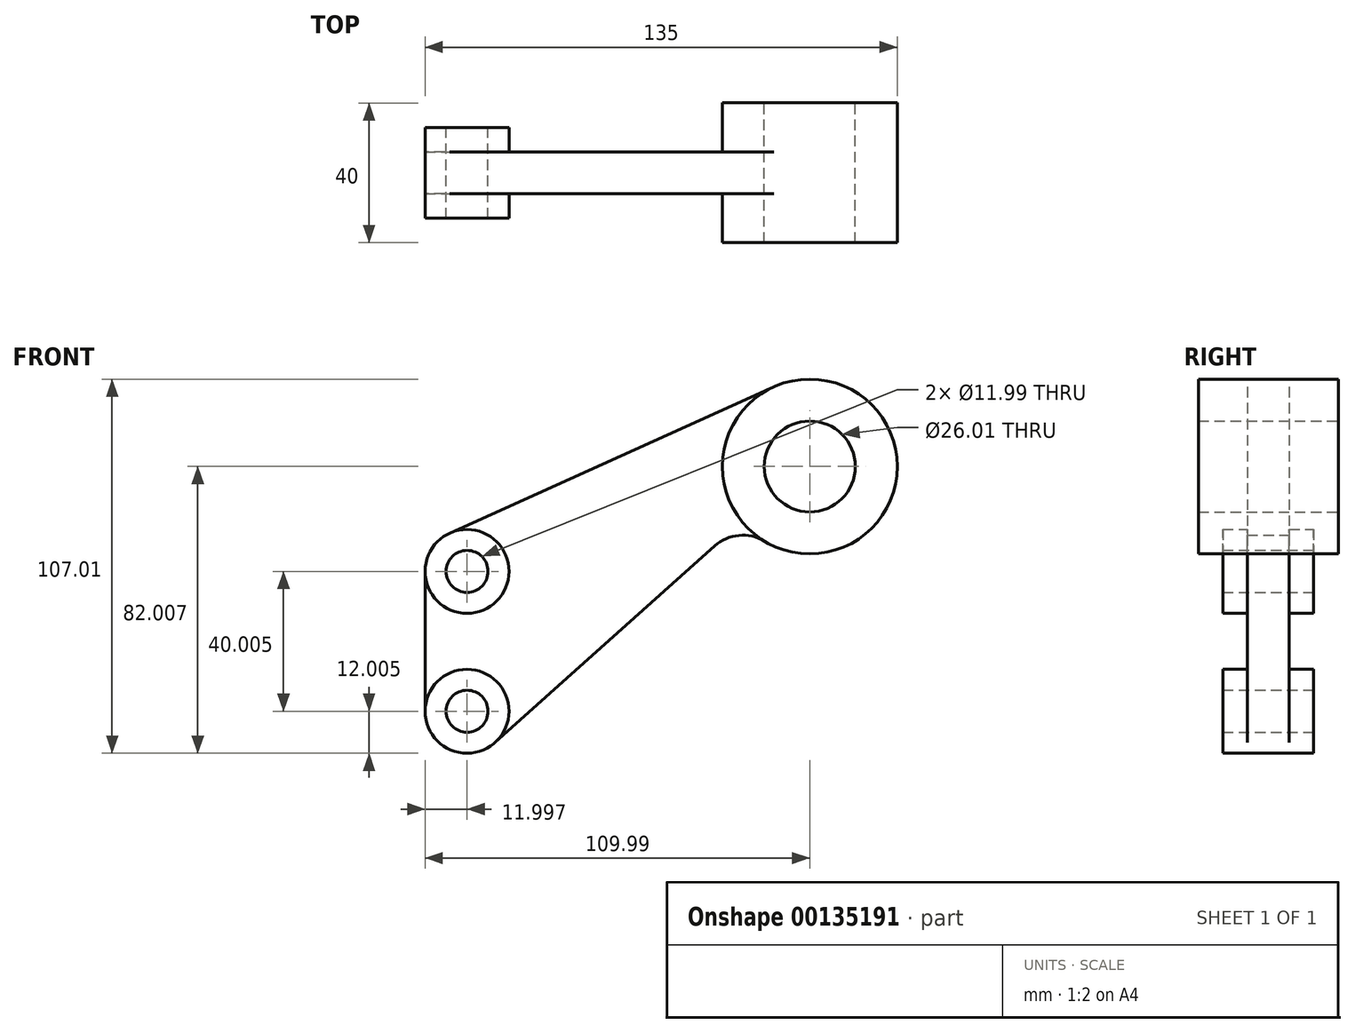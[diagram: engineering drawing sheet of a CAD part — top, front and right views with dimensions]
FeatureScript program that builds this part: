
annotation { "Feature Type Name" : "Feature", "Feature Type Description" : "" }
export const myFeature = defineFeature(function(context is Context, id is Id, definition is map)
    precondition{}
    {
        {
            var Q0;
            Q0=qCreatedBy(makeId("Front.planeOp"),FACE);
            var sketch = newSketch(context, id + "F0", { "sketchPlane" : qUnion([Q0])});
            skCircle(sketch, "E0", {"center": v(0, 53.52) * mm, "radius": 25 * mm});
            skCircle(sketch, "E1", {"center": v(0, 53.52) * mm, "radius": 13 * mm});
            skCircle(sketch, "E2", {"center": v(-98, 23.52) * mm, "radius": 12 * mm});
            skCircle(sketch, "E3", {"center": v(-98, 23.52) * mm, "radius": 6 * mm});
            skLineSegment(sketch, "E4", {"start": v(-10.3, 76.3) * mm, "end": v(-102.93, 34.46) * mm});
            skCircle(sketch, "E5", {"center": v(-98, -16.49) * mm, "radius": 6 * mm});
            skCircle(sketch, "E6", {"center": v(-98, -16.49) * mm, "radius": 12 * mm});
            skLineSegment(sketch, "E7", {"start": v(-110, 23.52) * mm, "end": v(-110, -16.49) * mm});
            skArc(sketch, "E8", {"start": v(-12.95, 32.12) * mm, "mid": v(-20.27, 33.8) * mm, "end": v(-27.15, 30.8) * mm});
            skLineSegment(sketch, "E9", {"start": v(-90, -25.43) * mm, "end": v(-27.15, 30.8) * mm});
            skSolve(sketch);
        }
        {
            var Q0;
            {var subQ3=sQuery(id+"F0.wireOp",EDGE,"E4");Q0=makeQuery(id+"F0.imprint","IMPRINT",FACE,{"disambiguationData":[TD([[makeQuery(id+"F0.imprint","IMPRINT",EDGE,{"derivedFrom":subQ3}),1.0]])]});}
            extrude(context, id + "F1", {"entities" : qUnion([Q0]), "endBound" : BoundingType.SYMMETRIC, "depth" : 12 * mm});
        }
        {
            var Q0;
            Q0=makeQuery(id+"F0.imprint","IMPRINT",FACE,{"disambiguationData":[TD([[makeQuery(id+"F0.imprint","IMPRINT",EDGE,{"derivedFrom":sQuery(id+"F0.wireOp",EDGE,"E1")}),-1.0]])]});
            extrude(context, id + "F2", {"entities" : qUnion([Q0]), "operationType" : NewBodyOperationType.ADD, "endBound" : BoundingType.SYMMETRIC, "depth" : 40 * mm});
        }
        {
            var Q0;
            Q0=makeQuery(id+"F0.imprint","IMPRINT",FACE,{"disambiguationData":[TD([[makeQuery(id+"F0.imprint","IMPRINT",EDGE,{"derivedFrom":sQuery(id+"F0.wireOp",EDGE,"E3")}),-1.0]])]});
            var Q1;
            Q1=makeQuery(id+"F0.imprint","IMPRINT",FACE,{"disambiguationData":[TD([[makeQuery(id+"F0.imprint","IMPRINT",EDGE,{"derivedFrom":sQuery(id+"F0.wireOp",EDGE,"E5")}),-1.0]])]});
            extrude(context, id + "F3", {"entities" : qUnion([Q0, Q1]), "operationType" : NewBodyOperationType.ADD, "endBound" : BoundingType.SYMMETRIC, "depth" : 26 * mm});
        }
    });
